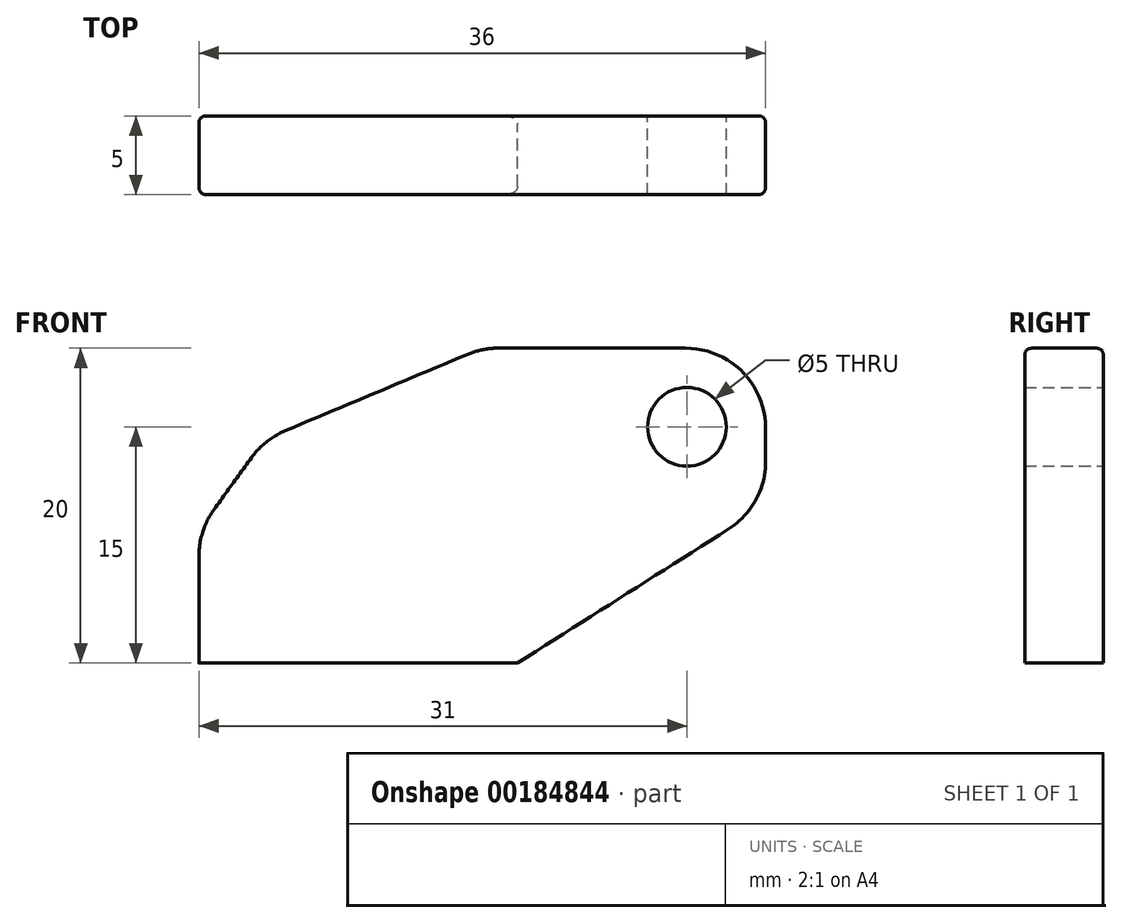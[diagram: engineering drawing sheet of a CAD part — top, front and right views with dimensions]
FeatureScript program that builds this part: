
annotation { "Feature Type Name" : "Feature", "Feature Type Description" : "" }
export const myFeature = defineFeature(function(context is Context, id is Id, definition is map)
    precondition{}
    {
        {
            var Q0;
            Q0=qCreatedBy(makeId("Front.planeOp"),FACE);
            var sketch = newSketch(context, id + "F0", { "sketchPlane" : qUnion([Q0])});
            skLineSegment(sketch, "E0.bottom", {"start": v(0, 0) * mm, "end": v(20.24, 0) * mm});
            skLineSegment(sketch, "E0.top", {"start": v(18, 20) * mm, "end": v(36, 20) * mm});
            skLineSegment(sketch, "E0.left", {"start": v(0, 0) * mm, "end": v(0, 8.42) * mm});
            skLineSegment(sketch, "E0.right", {"start": v(36, 10) * mm, "end": v(36, 20) * mm});
            skLineSegment(sketch, "E1", {"start": v(4.18, 14.2) * mm, "end": v(0, 8.42) * mm});
            skLineSegment(sketch, "E2", {"start": v(36, 10) * mm, "end": v(20.24, 0) * mm});
            skLineSegment(sketch, "E3", {"start": v(18, 20) * mm, "end": v(4.18, 14.2) * mm});
            skPoint(sketch, "E4.orphan", {"position": v(0, 20) * mm});
            skPoint(sketch, "E5.orphan", {"position": v(8.37, 20) * mm});
            skLineSegment(sketch, "E6", {"start": v(36, 10) * mm, "end": v(0, 10) * mm, "construction": true});
            skPoint(sketch, "E7.oppositeSnap0", {"position": v(27, 20) * mm});
            skLineSegment(sketch, "E7.bottom", {"start": v(27, 20) * mm, "end": v(27, 20) * mm});
            skLineSegment(sketch, "E7.top", {"start": v(27, 10) * mm, "end": v(27, 10) * mm});
            skLineSegment(sketch, "E7.left", {"start": v(27, 20) * mm, "end": v(27, 10) * mm, "construction": true});
            skLineSegment(sketch, "E7.right", {"start": v(27, 20) * mm, "end": v(27, 10) * mm, "construction": true});
            skLineSegment(sketch, "E8", {"start": v(36, 10) * mm, "end": v(26, 10) * mm, "construction": true});
            skLineSegment(sketch, "E9", {"start": v(36, 20) * mm, "end": v(26, 10) * mm, "construction": true});
            skLineSegment(sketch, "E10", {"start": v(26, 10) * mm, "end": v(26, 20) * mm, "construction": true});
            skLineSegment(sketch, "E11", {"start": v(26, 20) * mm, "end": v(36, 10) * mm, "construction": true});
            skCircle(sketch, "E12", {"center": v(31, 15) * mm, "radius": 2.5 * mm});
            skPoint(sketch, "E13.orphan", {"position": v(36, 0) * mm});
            skLineSegment(sketch, "E14", {"start": v(18, 20) * mm, "end": v(26, 10) * mm});
            skLineSegment(sketch, "E15", {"start": v(20.24, 0) * mm, "end": v(26, 10) * mm});
            skSolve(sketch);
        }
        {
            var Q0;
            Q0=makeQuery(id+"F0.imprint","IMPRINT",FACE,{"disambiguationData":[TD([[makeQuery(id+"F0.imprint","IMPRINT",EDGE,{"derivedFrom":sQuery(id+"F0.wireOp",EDGE,"E0.bottom")}),1.0]])]});
            extrude(context, id + "F1", {"entities" : qUnion([Q0]), "depth" : 5 * mm});
        }
        {
            var Q0;
            Q0=makeQuery(id+"F0.imprint","IMPRINT",FACE,{"disambiguationData":[TD([[makeQuery(id+"F0.imprint","IMPRINT",EDGE,{"derivedFrom":sQuery(id+"F0.wireOp",EDGE,"E0.bottom")}),1.0]])]});
            var Q1;
            Q1=makeQuery(id+"F0.imprint","IMPRINT",FACE,{"disambiguationData":[TD([[makeQuery(id+"F0.imprint","IMPRINT",EDGE,{"derivedFrom":sQuery(id+"F0.wireOp",EDGE,"E0.top")}),-1.0]])]});
            extrude(context, id + "F2", {"entities" : qUnion([Q0, Q1]), "operationType" : NewBodyOperationType.ADD, "depth" : 5 * mm});
        }
        {
            var Q0;
            Q0=makeQuery(id+"F2.opExtrude","SWEPT_EDGE",EDGE,{"disambiguationData":[OSD([sQuery(id+"F0.wireOp",EDGE,"E0.top"),sQuery(id+"F0.wireOp",EDGE,"E0.right")])]});
            var Q1;
            Q1=makeQuery(id+"F2.opExtrude","SWEPT_EDGE",EDGE,{"disambiguationData":[OSD([sQuery(id+"F0.wireOp",EDGE,"E0.right"),sQuery(id+"F0.wireOp",EDGE,"E2")])]});
            var Q2;
            {var subQ0=sQuery(id+"F0.wireOp",EDGE,"E14");var subQ1=sQuery(id+"F0.wireOp",EDGE,"E3");var subQ2=sQuery(id+"F0.wireOp",EDGE,"E0.top");Q2=makeQuery(id+"F2.boolean.opBoolean","MERGE",EDGE,{"derivedFrom":[makeQuery(id+"F1.opExtrude","SWEPT_EDGE",EDGE,{"disambiguationData":[OSD([subQ2,subQ1,subQ0])]}),makeQuery(id+"F2.opExtrude","SWEPT_EDGE",EDGE,{"disambiguationData":[OSD([subQ2,subQ1,subQ0])]})]});}
            var Q3;
            Q3=makeQuery(id+"F1.opExtrude","SWEPT_EDGE",EDGE,{"disambiguationData":[OSD([sQuery(id+"F0.wireOp",EDGE,"E1"),sQuery(id+"F0.wireOp",EDGE,"E3")])]});
            var Q4;
            Q4=makeQuery(id+"F1.opExtrude","SWEPT_EDGE",EDGE,{"disambiguationData":[OSD([sQuery(id+"F0.wireOp",EDGE,"E0.left"),sQuery(id+"F0.wireOp",EDGE,"E1")])]});
            fillet(context, id + "F3", {"entities" : qUnion([Q0, Q1, Q2, Q3, Q4]), "radius" : 5.08 * mm, "tangentPropagation" : true, "allowEdgeOverflow" : false});
        }
        {
            var Q0;
            Q0=makeQuery(id+"F2.opExtrude","CAP_EDGE",EDGE,{"disambiguationData":[OSD([sQuery(id+"F0.wireOp",EDGE,"E0.top")])],"isStart":false});
            var Q1;
            Q1=makeQuery(id+"F1.opExtrude","CAP_EDGE",EDGE,{"disambiguationData":[OSD([sQuery(id+"F0.wireOp",EDGE,"E3")])],"isStart":false});
            var Q2;
            Q2=makeQuery(id+"F2.opExtrude","CAP_EDGE",EDGE,{"disambiguationData":[OSD([sQuery(id+"F0.wireOp",EDGE,"E0.top")])],"isStart":true});
            var Q3;
            {var subQ0=sQuery(id+"F0.wireOp",EDGE,"E3");var subQ1=sQuery(id+"F0.wireOp",EDGE,"E1");var subQ2=sQuery(id+"F0.wireOp",EDGE,"E0.left");var subQ3=sQuery(id+"F0.wireOp",EDGE,"E0.top");var subQ4=sQuery(id+"F0.wireOp",EDGE,"E0.bottom");var subQ5=sQuery(id+"F0.wireOp",EDGE,"E14");Q3=makeQuery(id+"F3.opFillet","BLEND_EDGE",EDGE,{"blendedFrom":[makeQuery(id+"F2.boolean.opBoolean","MERGE",EDGE,{"derivedFrom":[makeQuery(id+"F1.opExtrude","SWEPT_EDGE",EDGE,{"disambiguationData":[OSD([subQ3,subQ0,subQ5])]}),makeQuery(id+"F2.opExtrude","SWEPT_EDGE",EDGE,{"disambiguationData":[OSD([subQ3,subQ0,subQ5])]})]}),makeQuery(id+"F2.boolean.opBoolean","MERGE",FACE,{"derivedFrom":[makeQuery(id+"F1.opExtrude","CAP_FACE",FACE,{"disambiguationData":[OSD([subQ4,subQ2,subQ1,subQ0,subQ5,sQuery(id+"F0.wireOp",EDGE,"E15")])],"isStart":true}),makeQuery(id+"F2.opExtrude","CAP_FACE",FACE,{"disambiguationData":[OSD([subQ4,subQ3,subQ2,sQuery(id+"F0.wireOp",EDGE,"E0.right"),subQ1,sQuery(id+"F0.wireOp",EDGE,"E2"),subQ0,sQuery(id+"F0.wireOp",EDGE,"E12")])],"isStart":true})]})],"blendedInto":[makeQuery(id+"F2.boolean.opBoolean","MERGE",FACE,{"derivedFrom":[makeQuery(id+"F1.opExtrude","CAP_FACE",FACE,{"disambiguationData":[OSD([subQ4,subQ2,subQ1,subQ0,subQ5,sQuery(id+"F0.wireOp",EDGE,"E15")])],"isStart":true}),makeQuery(id+"F2.opExtrude","CAP_FACE",FACE,{"disambiguationData":[OSD([subQ4,subQ3,subQ2,sQuery(id+"F0.wireOp",EDGE,"E0.right"),subQ1,sQuery(id+"F0.wireOp",EDGE,"E2"),subQ0,sQuery(id+"F0.wireOp",EDGE,"E12")])],"isStart":true})]})]});}
            var Q4;
            Q4=makeQuery(id+"F1.opExtrude","CAP_EDGE",EDGE,{"disambiguationData":[OSD([sQuery(id+"F0.wireOp",EDGE,"E3")])],"isStart":true});
            var Q5;
            {var subQ0=sQuery(id+"F0.wireOp",EDGE,"E3");var subQ1=sQuery(id+"F0.wireOp",EDGE,"E1");var subQ2=sQuery(id+"F0.wireOp",EDGE,"E0.right");var subQ3=sQuery(id+"F0.wireOp",EDGE,"E0.left");var subQ4=sQuery(id+"F0.wireOp",EDGE,"E0.top");var subQ5=sQuery(id+"F0.wireOp",EDGE,"E0.bottom");Q5=makeQuery(id+"F3.opFillet","BLEND_EDGE",EDGE,{"blendedFrom":[makeQuery(id+"F2.opExtrude","SWEPT_EDGE",EDGE,{"disambiguationData":[OSD([subQ4,subQ2])]}),makeQuery(id+"F2.boolean.opBoolean","MERGE",FACE,{"derivedFrom":[makeQuery(id+"F1.opExtrude","CAP_FACE",FACE,{"disambiguationData":[OSD([subQ5,subQ3,subQ1,subQ0,sQuery(id+"F0.wireOp",EDGE,"E14"),sQuery(id+"F0.wireOp",EDGE,"E15")])],"isStart":false}),makeQuery(id+"F2.opExtrude","CAP_FACE",FACE,{"disambiguationData":[OSD([subQ5,subQ4,subQ3,subQ2,subQ1,sQuery(id+"F0.wireOp",EDGE,"E2"),subQ0,sQuery(id+"F0.wireOp",EDGE,"E12")])],"isStart":false})]})],"blendedInto":[makeQuery(id+"F2.boolean.opBoolean","MERGE",FACE,{"derivedFrom":[makeQuery(id+"F1.opExtrude","CAP_FACE",FACE,{"disambiguationData":[OSD([subQ5,subQ3,subQ1,subQ0,sQuery(id+"F0.wireOp",EDGE,"E14"),sQuery(id+"F0.wireOp",EDGE,"E15")])],"isStart":false}),makeQuery(id+"F2.opExtrude","CAP_FACE",FACE,{"disambiguationData":[OSD([subQ5,subQ4,subQ3,subQ2,subQ1,sQuery(id+"F0.wireOp",EDGE,"E2"),subQ0,sQuery(id+"F0.wireOp",EDGE,"E12")])],"isStart":false})]})]});}
            var Q6;
            {var subQ0=sQuery(id+"F0.wireOp",EDGE,"E3");var subQ1=sQuery(id+"F0.wireOp",EDGE,"E1");var subQ2=sQuery(id+"F0.wireOp",EDGE,"E0.right");var subQ3=sQuery(id+"F0.wireOp",EDGE,"E0.left");var subQ4=sQuery(id+"F0.wireOp",EDGE,"E0.top");var subQ5=sQuery(id+"F0.wireOp",EDGE,"E0.bottom");Q6=makeQuery(id+"F3.opFillet","BLEND_EDGE",EDGE,{"blendedFrom":[makeQuery(id+"F2.opExtrude","SWEPT_EDGE",EDGE,{"disambiguationData":[OSD([subQ4,subQ2])]}),makeQuery(id+"F2.boolean.opBoolean","MERGE",FACE,{"derivedFrom":[makeQuery(id+"F1.opExtrude","CAP_FACE",FACE,{"disambiguationData":[OSD([subQ5,subQ3,subQ1,subQ0,sQuery(id+"F0.wireOp",EDGE,"E14"),sQuery(id+"F0.wireOp",EDGE,"E15")])],"isStart":true}),makeQuery(id+"F2.opExtrude","CAP_FACE",FACE,{"disambiguationData":[OSD([subQ5,subQ4,subQ3,subQ2,subQ1,sQuery(id+"F0.wireOp",EDGE,"E2"),subQ0,sQuery(id+"F0.wireOp",EDGE,"E12")])],"isStart":true})]})],"blendedInto":[makeQuery(id+"F2.boolean.opBoolean","MERGE",FACE,{"derivedFrom":[makeQuery(id+"F1.opExtrude","CAP_FACE",FACE,{"disambiguationData":[OSD([subQ5,subQ3,subQ1,subQ0,sQuery(id+"F0.wireOp",EDGE,"E14"),sQuery(id+"F0.wireOp",EDGE,"E15")])],"isStart":true}),makeQuery(id+"F2.opExtrude","CAP_FACE",FACE,{"disambiguationData":[OSD([subQ5,subQ4,subQ3,subQ2,subQ1,sQuery(id+"F0.wireOp",EDGE,"E2"),subQ0,sQuery(id+"F0.wireOp",EDGE,"E12")])],"isStart":true})]})]});}
            fillet(context, id + "F4", {"entities" : qUnion([Q0, Q1, Q2, Q3, Q4, Q5, Q6]), "radius" : 0.5 * mm, "tangentPropagation" : true, "rho" : 0.5, "crossSection" : FilletCrossSection.CONIC, "allowEdgeOverflow" : false});
        }
    });
